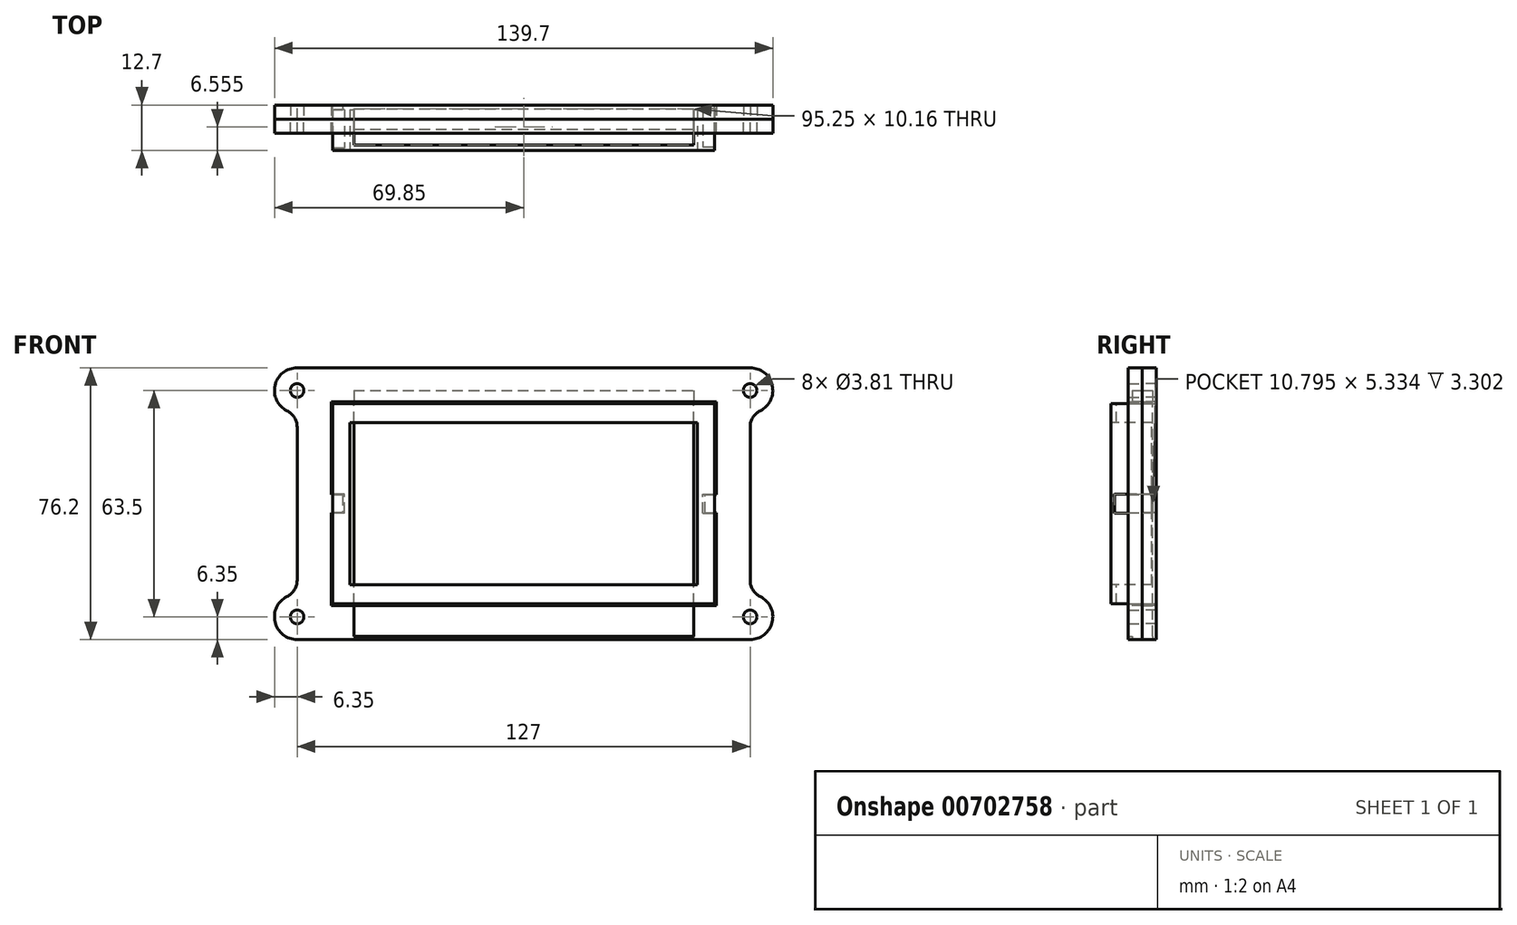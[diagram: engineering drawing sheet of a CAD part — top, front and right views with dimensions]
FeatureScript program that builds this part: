
annotation { "Feature Type Name" : "Feature", "Feature Type Description" : "" }
export const myFeature = defineFeature(function(context is Context, id is Id, definition is map)
    precondition{}
    {
        {
            var Q0;
            Q0=qCreatedBy(makeId("Front.planeOp"),FACE);
            var sketch = newSketch(context, id + "F0", { "sketchPlane" : qUnion([Q0])});
            skLineSegment(sketch, "E0.bottom", {"start": v(63.5, -38.1) * mm, "end": v(-63.5, -38.1) * mm});
            skLineSegment(sketch, "E0.top", {"start": v(63.5, 38.1) * mm, "end": v(-63.5, 38.1) * mm});
            skLineSegment(sketch, "E0.left", {"start": v(63.5, -38.1) * mm, "end": v(63.5, 38.1) * mm});
            skLineSegment(sketch, "E0.right", {"start": v(-63.5, -38.1) * mm, "end": v(-63.5, 38.1) * mm});
            skPoint(sketch, "E0.middle", {"position": v(0, 0) * mm});
            skSolve(sketch);
        }
        {
            var Q0;
            Q0 = qSketchRegion(id + "F0", true);
            extrude(context, id + "F1", {"entities" : qUnion([Q0]), "depth" : 3.94 * mm, "offsetDistance" : 25.4 * mm});
        }
        {
            var Q0;
            Q0=makeQuery(id+"F1.opExtrude","CAP_FACE",FACE,{"disambiguationData":[OSD([sQuery(id+"F0.wireOp",EDGE,"E0.bottom"),sQuery(id+"F0.wireOp",EDGE,"E0.top"),sQuery(id+"F0.wireOp",EDGE,"E0.left"),sQuery(id+"F0.wireOp",EDGE,"E0.right")])],"isStart":false});
            var sketch = newSketch(context, id + "F2", { "sketchPlane" : qUnion([Q0])});
            skLineSegment(sketch, "E1.bottom", {"start": v(-53.98, -28.58) * mm, "end": v(53.98, -28.58) * mm});
            skLineSegment(sketch, "E1.top", {"start": v(-53.98, 28.58) * mm, "end": v(53.98, 28.58) * mm});
            skLineSegment(sketch, "E1.left", {"start": v(-53.98, -28.58) * mm, "end": v(-53.98, 28.58) * mm});
            skLineSegment(sketch, "E1.right", {"start": v(53.98, -28.58) * mm, "end": v(53.98, 28.58) * mm});
            skPoint(sketch, "E1.middle", {"position": v(0, 0) * mm});
            skSolve(sketch);
        }
        {
            var Q0;
            Q0 = qSketchRegion(id + "F2", true);
            extrude(context, id + "F3", {"entities" : qUnion([Q0]), "operationType" : NewBodyOperationType.REMOVE, "oppositeDirection" : true, "depth" : 25.4 * mm, "offsetDistance" : 25.4 * mm});
        }
        {
            var Q0;
            Q0=makeQuery(id+"F1.opExtrude","CAP_FACE",FACE,{"disambiguationData":[OSD([sQuery(id+"F0.wireOp",EDGE,"E0.bottom"),sQuery(id+"F0.wireOp",EDGE,"E0.top"),sQuery(id+"F0.wireOp",EDGE,"E0.left"),sQuery(id+"F0.wireOp",EDGE,"E0.right")])],"isStart":false});
            var sketch = newSketch(context, id + "F4", { "sketchPlane" : qUnion([Q0])});
            skCircle(sketch, "E2", {"center": v(-63.5, 31.75) * mm, "radius": 6.35 * mm});
            skCircle(sketch, "E3", {"center": v(63.5, 31.75) * mm, "radius": 6.35 * mm});
            skCircle(sketch, "E4", {"center": v(-63.5, -31.75) * mm, "radius": 6.35 * mm});
            skCircle(sketch, "E5", {"center": v(63.5, -31.75) * mm, "radius": 6.35 * mm});
            skSolve(sketch);
        }
        {
            var Q0;
            Q0 = qSketchRegion(id + "F4", true);
            extrude(context, id + "F5", {"entities" : qUnion([Q0]), "operationType" : NewBodyOperationType.ADD, "oppositeDirection" : true, "depth" : 3.94 * mm, "offsetDistance" : 25.4 * mm});
        }
        {
            var Q0;
            Q0=makeQuery(id+"F5.boolean.opBoolean","INTERSECT",EDGE,{"derivedFrom":[makeQuery(id+"F1.opExtrude","SWEPT_FACE",FACE,{"disambiguationData":[OSD([sQuery(id+"F0.wireOp",EDGE,"E0.right")])]}),makeQuery(id+"F5.opExtrude","SWEPT_FACE",FACE,{"disambiguationData":[OSD([sQuery(id+"F4.wireOp",EDGE,"E2")])]})]});
            var Q1;
            Q1=makeQuery(id+"F5.boolean.opBoolean","INTERSECT",EDGE,{"derivedFrom":[makeQuery(id+"F1.opExtrude","SWEPT_FACE",FACE,{"disambiguationData":[OSD([sQuery(id+"F0.wireOp",EDGE,"E0.right")])]}),makeQuery(id+"F5.opExtrude","SWEPT_FACE",FACE,{"disambiguationData":[OSD([sQuery(id+"F4.wireOp",EDGE,"E4")])]})]});
            var Q2;
            Q2=makeQuery(id+"F5.boolean.opBoolean","INTERSECT",EDGE,{"derivedFrom":[makeQuery(id+"F1.opExtrude","SWEPT_FACE",FACE,{"disambiguationData":[OSD([sQuery(id+"F0.wireOp",EDGE,"E0.left")])]}),makeQuery(id+"F5.opExtrude","SWEPT_FACE",FACE,{"disambiguationData":[OSD([sQuery(id+"F4.wireOp",EDGE,"E3")])]})]});
            var Q3;
            Q3=makeQuery(id+"F5.boolean.opBoolean","INTERSECT",EDGE,{"derivedFrom":[makeQuery(id+"F1.opExtrude","SWEPT_FACE",FACE,{"disambiguationData":[OSD([sQuery(id+"F0.wireOp",EDGE,"E0.left")])]}),makeQuery(id+"F5.opExtrude","SWEPT_FACE",FACE,{"disambiguationData":[OSD([sQuery(id+"F4.wireOp",EDGE,"E5")])]})]});
            fillet(context, id + "F6", {"entities" : qUnion([Q0, Q1, Q2, Q3]), "radius" : 5.08 * mm, "tangentPropagation" : true, "allowEdgeOverflow" : false});
        }
        {
            var Q0;
            Q0=makeQuery(id+"F5.boolean.opBoolean","MERGE",FACE,{"derivedFrom":[makeQuery(id+"F1.opExtrude","CAP_FACE",FACE,{"disambiguationData":[OSD([sQuery(id+"F0.wireOp",EDGE,"E0.bottom"),sQuery(id+"F0.wireOp",EDGE,"E0.top"),sQuery(id+"F0.wireOp",EDGE,"E0.left"),sQuery(id+"F0.wireOp",EDGE,"E0.right")])],"isStart":false}),makeQuery(id+"F5.opExtrude","CAP_FACE",FACE,{"disambiguationData":[OSD([sQuery(id+"F4.wireOp",EDGE,"E2")])],"isStart":true}),makeQuery(id+"F5.opExtrude","CAP_FACE",FACE,{"disambiguationData":[OSD([sQuery(id+"F4.wireOp",EDGE,"E3")])],"isStart":true}),makeQuery(id+"F5.opExtrude","CAP_FACE",FACE,{"disambiguationData":[OSD([sQuery(id+"F4.wireOp",EDGE,"E4")])],"isStart":true}),makeQuery(id+"F5.opExtrude","CAP_FACE",FACE,{"disambiguationData":[OSD([sQuery(id+"F4.wireOp",EDGE,"E5")])],"isStart":true})]});
            var sketch = newSketch(context, id + "F7", { "sketchPlane" : qUnion([Q0])});
            skCircle(sketch, "E6", {"center": v(-63.5, 31.75) * mm, "radius": 1.9 * mm});
            skCircle(sketch, "E7", {"center": v(-63.5, -31.75) * mm, "radius": 1.9 * mm});
            skCircle(sketch, "E8", {"center": v(63.5, -31.75) * mm, "radius": 1.9 * mm});
            skCircle(sketch, "E9", {"center": v(63.5, 31.75) * mm, "radius": 1.9 * mm});
            skSolve(sketch);
        }
        {
            var Q0;
            Q0 = qSketchRegion(id + "F7", true);
            extrude(context, id + "F8", {"entities" : qUnion([Q0]), "operationType" : NewBodyOperationType.REMOVE, "oppositeDirection" : true, "depth" : 25.4 * mm, "offsetDistance" : 25.4 * mm});
        }
        {
            var Q0;
            Q0=makeQuery(id+"F5.boolean.opBoolean","MERGE",FACE,{"derivedFrom":[makeQuery(id+"F1.opExtrude","CAP_FACE",FACE,{"disambiguationData":[OSD([sQuery(id+"F0.wireOp",EDGE,"E0.bottom"),sQuery(id+"F0.wireOp",EDGE,"E0.top"),sQuery(id+"F0.wireOp",EDGE,"E0.left"),sQuery(id+"F0.wireOp",EDGE,"E0.right")])],"isStart":false}),makeQuery(id+"F5.opExtrude","CAP_FACE",FACE,{"disambiguationData":[OSD([sQuery(id+"F4.wireOp",EDGE,"E2")])],"isStart":true}),makeQuery(id+"F5.opExtrude","CAP_FACE",FACE,{"disambiguationData":[OSD([sQuery(id+"F4.wireOp",EDGE,"E3")])],"isStart":true}),makeQuery(id+"F5.opExtrude","CAP_FACE",FACE,{"disambiguationData":[OSD([sQuery(id+"F4.wireOp",EDGE,"E4")])],"isStart":true}),makeQuery(id+"F5.opExtrude","CAP_FACE",FACE,{"disambiguationData":[OSD([sQuery(id+"F4.wireOp",EDGE,"E5")])],"isStart":true})]});
            var sketch = newSketch(context, id + "F9", { "sketchPlane" : qUnion([Q0])});
            skLineSegment(sketch, "E10.bottom", {"start": v(-50.8, -2.54) * mm, "end": v(-53.98, -2.54) * mm});
            skLineSegment(sketch, "E10.top", {"start": v(-50.8, 2.54) * mm, "end": v(-53.98, 2.54) * mm});
            skLineSegment(sketch, "E10.left", {"start": v(-50.8, -2.54) * mm, "end": v(-50.8, 2.54) * mm});
            skLineSegment(sketch, "E10.right", {"start": v(-53.98, -2.54) * mm, "end": v(-53.98, 2.54) * mm});
            skPoint(sketch, "E10.middle", {"position": v(-52.39, 0) * mm});
            skLineSegment(sketch, "E11.bottom", {"start": v(50.8, -2.54) * mm, "end": v(53.98, -2.54) * mm});
            skLineSegment(sketch, "E11.top", {"start": v(50.8, 2.54) * mm, "end": v(53.98, 2.54) * mm});
            skLineSegment(sketch, "E11.left", {"start": v(50.8, -2.54) * mm, "end": v(50.8, 2.54) * mm});
            skLineSegment(sketch, "E11.right", {"start": v(53.98, -2.54) * mm, "end": v(53.98, 2.54) * mm});
            skPoint(sketch, "E11.middle", {"position": v(52.39, 0) * mm});
            skSolve(sketch);
        }
        {
            var Q0;
            Q0 = qSketchRegion(id + "F9", true);
            extrude(context, id + "F10", {"entities" : qUnion([Q0]), "operationType" : NewBodyOperationType.ADD, "oppositeDirection" : true, "depth" : 3.94 * mm, "offsetDistance" : 25.4 * mm});
        }
        {
            var Q0;
            Q0=makeQuery(id+"F10.boolean.opBoolean","MERGE",FACE,{"derivedFrom":[makeQuery(id+"F5.boolean.opBoolean","MERGE",FACE,{"derivedFrom":[makeQuery(id+"F1.opExtrude","CAP_FACE",FACE,{"disambiguationData":[OSD([sQuery(id+"F0.wireOp",EDGE,"E0.bottom"),sQuery(id+"F0.wireOp",EDGE,"E0.top"),sQuery(id+"F0.wireOp",EDGE,"E0.left"),sQuery(id+"F0.wireOp",EDGE,"E0.right")])],"isStart":false}),makeQuery(id+"F5.opExtrude","CAP_FACE",FACE,{"disambiguationData":[OSD([sQuery(id+"F4.wireOp",EDGE,"E2")])],"isStart":true}),makeQuery(id+"F5.opExtrude","CAP_FACE",FACE,{"disambiguationData":[OSD([sQuery(id+"F4.wireOp",EDGE,"E3")])],"isStart":true}),makeQuery(id+"F5.opExtrude","CAP_FACE",FACE,{"disambiguationData":[OSD([sQuery(id+"F4.wireOp",EDGE,"E4")])],"isStart":true}),makeQuery(id+"F5.opExtrude","CAP_FACE",FACE,{"disambiguationData":[OSD([sQuery(id+"F4.wireOp",EDGE,"E5")])],"isStart":true})]}),makeQuery(id+"F10.opExtrude","CAP_FACE",FACE,{"disambiguationData":[OSD([sQuery(id+"F9.wireOp",EDGE,"E10.bottom"),sQuery(id+"F9.wireOp",EDGE,"E10.top"),sQuery(id+"F9.wireOp",EDGE,"E10.left"),sQuery(id+"F9.wireOp",EDGE,"E10.right")])],"isStart":true}),makeQuery(id+"F10.opExtrude","CAP_FACE",FACE,{"disambiguationData":[OSD([sQuery(id+"F9.wireOp",EDGE,"E11.bottom"),sQuery(id+"F9.wireOp",EDGE,"E11.top"),sQuery(id+"F9.wireOp",EDGE,"E11.left"),sQuery(id+"F9.wireOp",EDGE,"E11.right")])],"isStart":true})]});
            extrude(context, id + "F11", {"entities" : qUnion([Q0]), "depth" : 3.94 * mm, "offsetDistance" : 25.4 * mm});
        }
        {
            var Q0;
            Q0=makeQuery(id+"F1.opExtrude","SWEPT_FACE",FACE,{"disambiguationData":[OSD([sQuery(id+"F0.wireOp",EDGE,"E0.bottom")])]});
            var sketch = newSketch(context, id + "F12", { "sketchPlane" : qUnion([Q0])});
            skLineSegment(sketch, "E12.bottom", {"start": v(-47.63, 6.8) * mm, "end": v(47.63, 6.8) * mm});
            skLineSegment(sketch, "E12.top", {"start": v(-47.63, 1.08) * mm, "end": v(47.63, 1.08) * mm});
            skLineSegment(sketch, "E12.left", {"start": v(-47.63, 6.8) * mm, "end": v(-47.63, 1.08) * mm});
            skLineSegment(sketch, "E12.right", {"start": v(47.63, 6.8) * mm, "end": v(47.63, 1.08) * mm});
            skPoint(sketch, "E12.middle", {"position": v(0, 3.94) * mm});
            skSolve(sketch);
        }
        {
            var Q0;
            Q0 = qSketchRegion(id + "F12", true);
            extrude(context, id + "F13", {"entities" : qUnion([Q0]), "operationType" : NewBodyOperationType.REMOVE, "oppositeDirection" : true, "depth" : 69.85 * mm, "offsetDistance" : 25.4 * mm});
        }
        {
            var Q0;
            Q0=qCreatedBy(makeId("Front.planeOp"),FACE);
            var sketch = newSketch(context, id + "F14", { "sketchPlane" : qUnion([Q0])});
            skLineSegment(sketch, "E13.bottom", {"start": v(-53.52, -28.1) * mm, "end": v(53.52, -28.1) * mm});
            skLineSegment(sketch, "E13.top", {"start": v(-53.52, 28.1) * mm, "end": v(53.52, 28.1) * mm});
            skLineSegment(sketch, "E13.left", {"start": v(-53.52, -28.1) * mm, "end": v(-53.52, 28.1) * mm});
            skLineSegment(sketch, "E13.right", {"start": v(53.52, -28.1) * mm, "end": v(53.52, 28.1) * mm});
            skPoint(sketch, "E13.middle", {"position": v(0, 0) * mm});
            skSolve(sketch);
        }
        {
            var Q0;
            Q0 = qSketchRegion(id + "F14", true);
            extrude(context, id + "F15", {"entities" : qUnion([Q0]), "depth" : 12.7 * mm, "offsetDistance" : 25.4 * mm});
        }
        {
            var Q0;
            Q0=makeQuery(id+"F15.opExtrude","CAP_FACE",FACE,{"disambiguationData":[OSD([sQuery(id+"F14.wireOp",EDGE,"E13.bottom"),sQuery(id+"F14.wireOp",EDGE,"E13.top"),sQuery(id+"F14.wireOp",EDGE,"E13.left"),sQuery(id+"F14.wireOp",EDGE,"E13.right")])],"isStart":false});
            var sketch = newSketch(context, id + "F16", { "sketchPlane" : qUnion([Q0])});
            skLineSegment(sketch, "E14.bottom", {"start": v(-48.7, -22.78) * mm, "end": v(48.7, -22.78) * mm});
            skLineSegment(sketch, "E14.top", {"start": v(-48.7, 22.78) * mm, "end": v(48.7, 22.78) * mm});
            skLineSegment(sketch, "E14.left", {"start": v(-48.7, -22.78) * mm, "end": v(-48.7, 22.78) * mm});
            skLineSegment(sketch, "E14.right", {"start": v(48.7, -22.78) * mm, "end": v(48.7, 22.78) * mm});
            skPoint(sketch, "E14.middle", {"position": v(0, 0) * mm});
            skSolve(sketch);
        }
        {
            var Q0;
            Q0 = qSketchRegion(id + "F16", true);
            extrude(context, id + "F17", {"entities" : qUnion([Q0]), "operationType" : NewBodyOperationType.REMOVE, "oppositeDirection" : true, "depth" : 11.43 * mm, "offsetDistance" : 25.4 * mm});
        }
        {
            var Q0;
            Q0=makeQuery(id+"F15.opExtrude","SWEPT_FACE",FACE,{"disambiguationData":[OSD([sQuery(id+"F14.wireOp",EDGE,"E13.top")])]});
            var sketch = newSketch(context, id + "F18", { "sketchPlane" : qUnion([Q0])});
            skPoint(sketch, "E15.middle", {"position": v(0, -6.14) * mm});
            skLineSegment(sketch, "E16.bottom", {"start": v(-47.63, -11.22) * mm, "end": v(47.63, -11.22) * mm});
            skLineSegment(sketch, "E16.top", {"start": v(-47.63, -1.06) * mm, "end": v(47.63, -1.06) * mm});
            skLineSegment(sketch, "E16.left", {"start": v(-47.63, -11.22) * mm, "end": v(-47.63, -1.06) * mm});
            skLineSegment(sketch, "E16.right", {"start": v(47.63, -11.22) * mm, "end": v(47.63, -1.06) * mm});
            skSolve(sketch);
        }
        {
            var Q0;
            Q0 = qSketchRegion(id + "F18", true);
            extrude(context, id + "F19", {"entities" : qUnion([Q0]), "operationType" : NewBodyOperationType.REMOVE, "oppositeDirection" : true, "depth" : 65.28 * mm, "offsetDistance" : 25.4 * mm});
        }
        {
            var Q0;
            Q0=makeQuery(id+"F15.opExtrude","SWEPT_FACE",FACE,{"disambiguationData":[OSD([sQuery(id+"F14.wireOp",EDGE,"E13.right")])]});
            var sketch = newSketch(context, id + "F20", { "sketchPlane" : qUnion([Q0])});
            skPoint(sketch, "E17.endSnap0", {"position": v(-12.7, 0) * mm});
            skLineSegment(sketch, "E18.bottom", {"start": v(-0.95, -2.67) * mm, "end": v(-11.75, -2.67) * mm});
            skLineSegment(sketch, "E18.top", {"start": v(-0.95, 2.67) * mm, "end": v(-11.75, 2.67) * mm});
            skLineSegment(sketch, "E18.left", {"start": v(-0.95, -2.67) * mm, "end": v(-0.95, 2.67) * mm});
            skLineSegment(sketch, "E18.right", {"start": v(-11.75, -2.67) * mm, "end": v(-11.75, 2.67) * mm});
            skPoint(sketch, "E18.middle", {"position": v(-6.35, 0) * mm});
            skSolve(sketch);
        }
        {
            var Q0;
            Q0 = qSketchRegion(id + "F20", true);
            extrude(context, id + "F21", {"entities" : qUnion([Q0]), "operationType" : NewBodyOperationType.REMOVE, "oppositeDirection" : true, "depth" : 3.3 * mm, "offsetDistance" : 25.4 * mm});
        }
        {
            var Q0;
            Q0=makeQuery(id+"F15.opExtrude","SWEPT_FACE",FACE,{"disambiguationData":[OSD([sQuery(id+"F14.wireOp",EDGE,"E13.left")])]});
            var sketch = newSketch(context, id + "F22", { "sketchPlane" : qUnion([Q0])});
            skLineSegment(sketch, "E19.bottom", {"start": v(1.27, -2.67) * mm, "end": v(12.06, -2.67) * mm});
            skLineSegment(sketch, "E19.top", {"start": v(1.27, 2.67) * mm, "end": v(12.06, 2.67) * mm});
            skLineSegment(sketch, "E19.left", {"start": v(1.27, -2.67) * mm, "end": v(1.27, 2.67) * mm});
            skLineSegment(sketch, "E19.right", {"start": v(12.06, -2.67) * mm, "end": v(12.06, 2.67) * mm});
            skPoint(sketch, "E19.middle", {"position": v(6.67, 0) * mm});
            skSolve(sketch);
        }
        {
            var Q0;
            Q0 = qSketchRegion(id + "F22", true);
            extrude(context, id + "F23", {"entities" : qUnion([Q0]), "operationType" : NewBodyOperationType.REMOVE, "oppositeDirection" : true, "depth" : 3.3 * mm, "offsetDistance" : 25.4 * mm});
        }
    });
